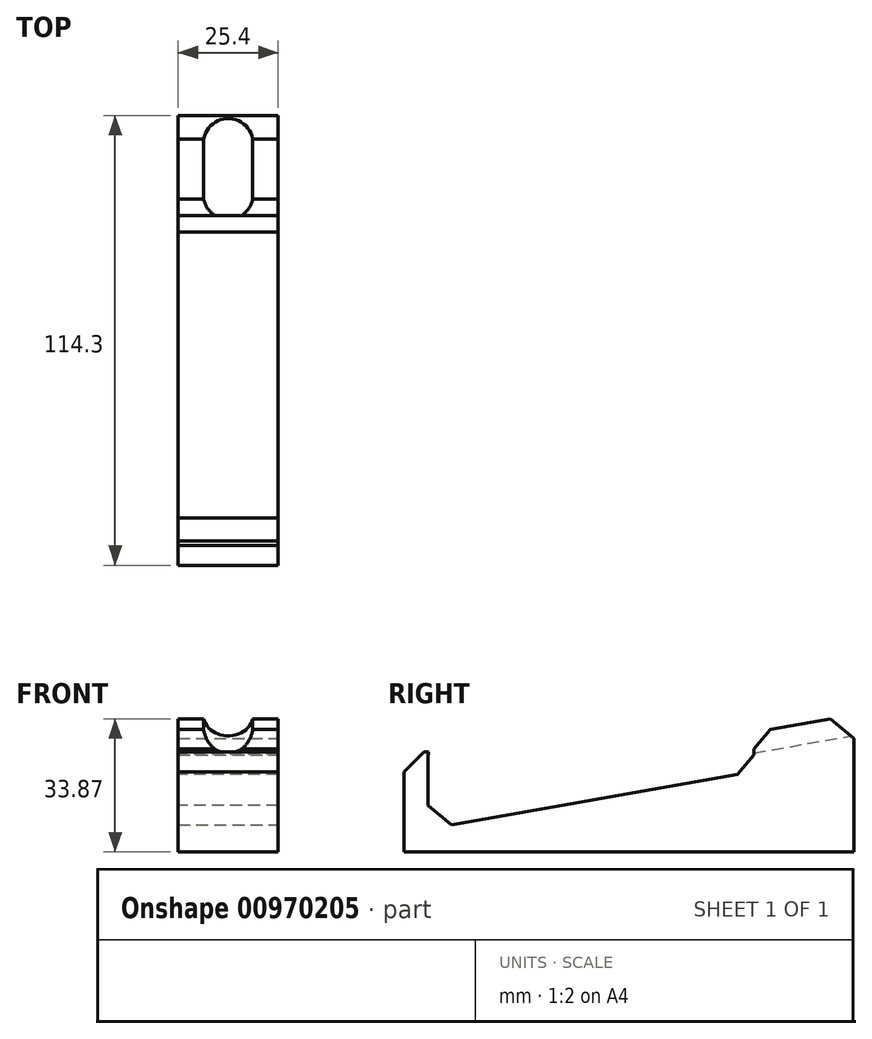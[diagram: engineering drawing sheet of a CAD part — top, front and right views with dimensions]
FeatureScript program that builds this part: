
annotation { "Feature Type Name" : "Feature", "Feature Type Description" : "" }
export const myFeature = defineFeature(function(context is Context, id is Id, definition is map)
    precondition{}
    {
        {
            var Q0;
            Q0=qCreatedBy(makeId("Right.planeOp"),FACE);
            var sketch = newSketch(context, id + "F0", { "sketchPlane" : qUnion([Q0])});
            skLineSegment(sketch, "E0", {"start": v(-114.3, 0) * mm, "end": v(0, 0) * mm});
            skLineSegment(sketch, "E1", {"start": v(0, 0) * mm, "end": v(0, 34.93) * mm});
            skLineSegment(sketch, "E2", {"start": v(0, 34.93) * mm, "end": v(-25.4, 30.45) * mm});
            skLineSegment(sketch, "E3", {"start": v(-25.4, 30.45) * mm, "end": v(-25.4, 20.46) * mm});
            skLineSegment(sketch, "E4", {"start": v(-25.4, 20.46) * mm, "end": v(-108.25, 5.85) * mm});
            skLineSegment(sketch, "E5", {"start": v(-108.25, 5.85) * mm, "end": v(-108.25, 24.83) * mm});
            skLineSegment(sketch, "E6", {"start": v(-108.13, 24.85) * mm, "end": v(-108.25, 24.83) * mm});
            skLineSegment(sketch, "E7", {"start": v(-108.13, 24.85) * mm, "end": v(-108.13, 25.4) * mm});
            skLineSegment(sketch, "E8", {"start": v(-108.13, 25.4) * mm, "end": v(-114.3, 25.4) * mm});
            skLineSegment(sketch, "E9", {"start": v(-114.3, 25.4) * mm, "end": v(-114.3, 0) * mm});
            skLineSegment(sketch, "E10", {"start": v(0, 34.93) * mm, "end": v(-114.3, 14.77) * mm, "construction": true});
            skSolve(sketch);
        }
        {
            var Q0;
            Q0=makeQuery(id+"F0.imprint","IMPRINT",FACE,{"disambiguationData":[TD([[makeQuery(id+"F0.imprint","IMPRINT",EDGE,{"derivedFrom":sQuery(id+"F0.wireOp",EDGE,"E0")}),1.0]])]});
            extrude(context, id + "F1", {"entities" : qUnion([Q0]), "endBound" : BoundingType.SYMMETRIC, "depth" : 25.4 * mm, "offsetDistance" : 25.4 * mm});
        }
        {
            var Q0;
            Q0=makeQuery(id+"F1.opExtrude","SWEPT_EDGE",EDGE,{"disambiguationData":[OSD([sQuery(id+"F0.wireOp",EDGE,"E1"),sQuery(id+"F0.wireOp",EDGE,"E2")])]});
            cPlane(context, id + "F2", {"entities" : qUnion([Q0]), "cplaneType" : CPlaneType.LINE_ANGLE, "offset" : 25.4 * mm, "angle" : 10 * degree, "oppositeDirection" : true, "width" : 152.4 * mm, "height" : 152.4 * mm});
        }
        {
            var Q0;
            Q0=qCreatedBy(id+"F2.planeOp",FACE);
            var sketch = newSketch(context, id + "F3", { "sketchPlane" : qUnion([Q0])});
            skCircle(sketch, "E11", {"center": v(0, 35.56) * mm, "radius": 6.35 * mm});
            skSolve(sketch);
        }
        {
            var Q0;
            Q0=makeQuery(id+"F3.imprint","IMPRINT",FACE,{"disambiguationData":[TD([[makeQuery(id+"F3.imprint","IMPRINT",EDGE,{"derivedFrom":sQuery(id+"F3.wireOp",EDGE,"E11")}),1.0]])]});
            extrude(context, id + "F4", {"entities" : qUnion([Q0]), "operationType" : NewBodyOperationType.REMOVE, "depth" : 104.14 * mm, "offsetDistance" : 25.4 * mm});
        }
        {
            var Q0;
            Q0=makeQuery(id+"F1.opExtrude","SWEPT_EDGE",EDGE,{"disambiguationData":[OSD([sQuery(id+"F0.wireOp",EDGE,"E8"),sQuery(id+"F0.wireOp",EDGE,"E9")])]});
            var Q1;
            {var subQ0=sQuery(id+"F0.wireOp",EDGE,"E2");var subQ1=sQuery(id+"F0.wireOp",EDGE,"E1");Q1=makeQuery(id+"F4.boolean.opBoolean","SPLIT",EDGE,{"disambiguationData":[TD([makeQuery(id+"F1.opExtrude","CAP_FACE",FACE,{"disambiguationData":[OSD([sQuery(id+"F0.wireOp",EDGE,"E0"),subQ1,subQ0,sQuery(id+"F0.wireOp",EDGE,"E3"),sQuery(id+"F0.wireOp",EDGE,"E4"),sQuery(id+"F0.wireOp",EDGE,"E5"),sQuery(id+"F0.wireOp",EDGE,"E6"),sQuery(id+"F0.wireOp",EDGE,"E7"),sQuery(id+"F0.wireOp",EDGE,"E8"),sQuery(id+"F0.wireOp",EDGE,"E9")])],"isStart":true})])],"derivedFrom":makeQuery(id+"F1.opExtrude","SWEPT_EDGE",EDGE,{"disambiguationData":[OSD([subQ1,subQ0])]})});}
            var Q2;
            Q2=makeQuery(id+"F1.opExtrude","SWEPT_EDGE",EDGE,{"disambiguationData":[OSD([sQuery(id+"F0.wireOp",EDGE,"E3"),sQuery(id+"F0.wireOp",EDGE,"E4")])]});
            var Q3;
            Q3=makeQuery(id+"F1.opExtrude","SWEPT_EDGE",EDGE,{"disambiguationData":[OSD([sQuery(id+"F0.wireOp",EDGE,"E4"),sQuery(id+"F0.wireOp",EDGE,"E5")])]});
            var Q4;
            {var subQ0=sQuery(id+"F0.wireOp",EDGE,"E3");var subQ1=sQuery(id+"F0.wireOp",EDGE,"E2");Q4=makeQuery(id+"F4.boolean.opBoolean","SPLIT",EDGE,{"disambiguationData":[TD([makeQuery(id+"F1.opExtrude","CAP_FACE",FACE,{"disambiguationData":[OSD([sQuery(id+"F0.wireOp",EDGE,"E0"),sQuery(id+"F0.wireOp",EDGE,"E1"),subQ1,subQ0,sQuery(id+"F0.wireOp",EDGE,"E4"),sQuery(id+"F0.wireOp",EDGE,"E5"),sQuery(id+"F0.wireOp",EDGE,"E6"),sQuery(id+"F0.wireOp",EDGE,"E7"),sQuery(id+"F0.wireOp",EDGE,"E8"),sQuery(id+"F0.wireOp",EDGE,"E9")])],"isStart":false})])],"derivedFrom":makeQuery(id+"F1.opExtrude","SWEPT_EDGE",EDGE,{"disambiguationData":[OSD([subQ1,subQ0])]})});}
            var Q5;
            {var subQ0=sQuery(id+"F0.wireOp",EDGE,"E3");var subQ1=sQuery(id+"F0.wireOp",EDGE,"E2");Q5=makeQuery(id+"F4.boolean.opBoolean","SPLIT",EDGE,{"disambiguationData":[TD([makeQuery(id+"F1.opExtrude","CAP_FACE",FACE,{"disambiguationData":[OSD([sQuery(id+"F0.wireOp",EDGE,"E0"),sQuery(id+"F0.wireOp",EDGE,"E1"),subQ1,subQ0,sQuery(id+"F0.wireOp",EDGE,"E4"),sQuery(id+"F0.wireOp",EDGE,"E5"),sQuery(id+"F0.wireOp",EDGE,"E6"),sQuery(id+"F0.wireOp",EDGE,"E7"),sQuery(id+"F0.wireOp",EDGE,"E8"),sQuery(id+"F0.wireOp",EDGE,"E9")])],"isStart":true})])],"derivedFrom":makeQuery(id+"F1.opExtrude","SWEPT_EDGE",EDGE,{"disambiguationData":[OSD([subQ1,subQ0])]})});}
            chamfer(context, id + "F5", {"entities" : qUnion([Q0, Q1, Q2, Q3, Q4, Q5]), "width" : 5.08 * mm, "tangentPropagation" : true});
        }
    });
